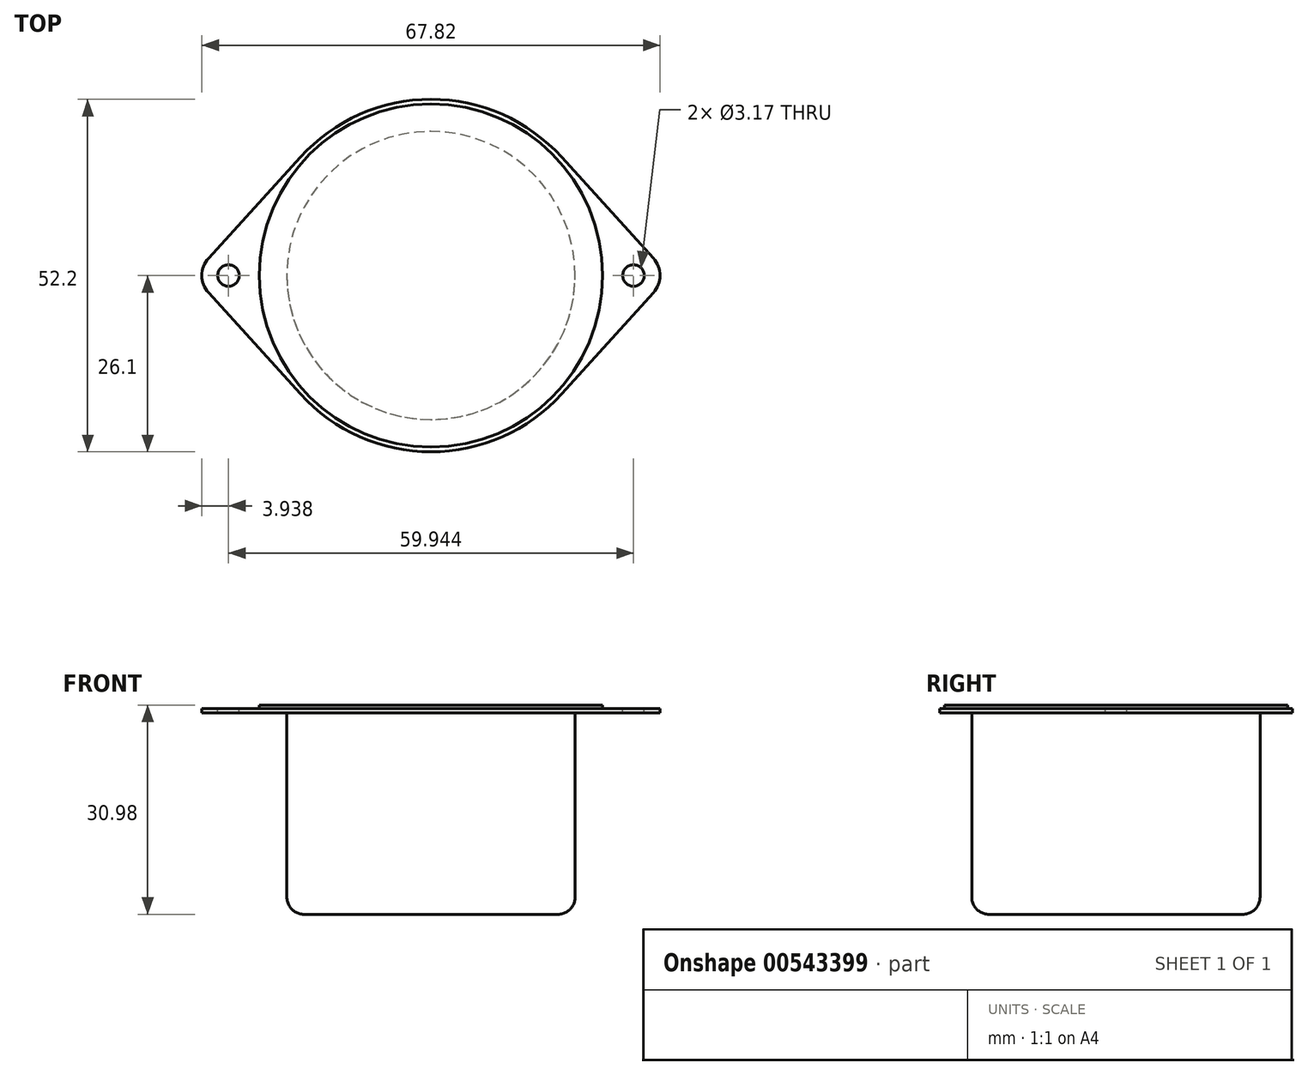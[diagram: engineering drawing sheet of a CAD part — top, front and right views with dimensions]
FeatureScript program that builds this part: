
annotation { "Feature Type Name" : "Feature", "Feature Type Description" : "" }
export const myFeature = defineFeature(function(context is Context, id is Id, definition is map)
    precondition{}
    {
        {
            var Q0;
            Q0=qCreatedBy(makeId("Front.planeOp"),FACE);
            var sketch = newSketch(context, id + "F0", { "sketchPlane" : qUnion([Q0])});
            skLineSegment(sketch, "E0", {"start": v(0, 46.59) * mm, "end": v(0, -54.94) * mm, "construction": true});
            skLineSegment(sketch, "E1", {"start": v(26.1, 14.99) * mm, "end": v(26.1, 14.35) * mm});
            skLineSegment(sketch, "E2", {"start": v(26.1, 14.35) * mm, "end": v(21.34, 14.35) * mm});
            skLineSegment(sketch, "E3", {"start": v(21.34, 14.35) * mm, "end": v(21.34, -15.5) * mm});
            skLineSegment(sketch, "E4", {"start": v(21.34, -15.5) * mm, "end": v(0, -15.5) * mm});
            skLineSegment(sketch, "E5", {"start": v(0, -15.5) * mm, "end": v(0, 15.5) * mm});
            skLineSegment(sketch, "E6", {"start": v(26.1, 14.99) * mm, "end": v(25.4, 14.99) * mm});
            skLineSegment(sketch, "E7", {"start": v(25.4, 14.99) * mm, "end": v(25.4, 15.5) * mm});
            skLineSegment(sketch, "E8", {"start": v(25.4, 15.5) * mm, "end": v(0, 15.5) * mm});
            skPoint(sketch, "E9.6.internal.snap0", {"position": v(12.7, 15.5) * mm});
            skSolve(sketch);
        }
        {
            var Q0;
            Q0 = qSketchRegion(id + "F0", true);
            var Q1;
            Q1=sQuery(id+"F0.wireOp",EDGE,"E0");
            revolve(context, id + "F1", {"entities" : qUnion([Q0]), "axis" : qUnion([Q1]), "revolveType" : RevolveType.FULL});
        }
        {
            var Q0;
            Q0=makeQuery(id+"F1.opRevolve","SWEPT_FACE",FACE,{"disambiguationData":[OSD([sQuery(id+"F0.wireOp",EDGE,"E6")])]});
            var sketch = newSketch(context, id + "F2", { "sketchPlane" : qUnion([Q0])});
            skCircle(sketch, "E10.0", {"center": v(0, 0) * mm, "radius": 26.1 * mm});
            skCircle(sketch, "E11", {"center": v(-30.1, 0) * mm, "radius": 3.81 * mm});
            skCircle(sketch, "E12", {"center": v(30.1, 0) * mm, "radius": 3.81 * mm});
            skLineSegment(sketch, "E13", {"start": v(-32.92, 2.56) * mm, "end": v(-19.33, 17.54) * mm});
            skLineSegment(sketch, "E14", {"start": v(-32.92, -2.56) * mm, "end": v(-19.33, -17.54) * mm});
            skLineSegment(sketch, "E15", {"start": v(32.92, -2.56) * mm, "end": v(19.33, -17.54) * mm});
            skLineSegment(sketch, "E16", {"start": v(32.92, 2.56) * mm, "end": v(19.33, 17.54) * mm});
            skLineSegment(sketch, "E17", {"start": v(0, 37.88) * mm, "end": v(0, -40.1) * mm, "construction": true});
            skCircle(sketch, "E18", {"center": v(-29.97, 0) * mm, "radius": 1.59 * mm});
            skCircle(sketch, "E19", {"center": v(29.97, 0) * mm, "radius": 1.59 * mm});
            skSolve(sketch);
        }
        {
            var Q0;
            Q0 = qSketchRegion(id + "F2", true);
            var Q1;
            Q1=makeQuery(id+"F1.opRevolve","SWEPT_FACE",FACE,{"disambiguationData":[OSD([sQuery(id+"F0.wireOp",EDGE,"E2")])]});
            extrude(context, id + "F3", {"entities" : qUnion([Q0]), "operationType" : NewBodyOperationType.ADD, "endBound" : BoundingType.UP_TO_SURFACE, "oppositeDirection" : true, "depth" : 25.4 * mm, "endBoundEntityFace" : qUnion([Q1]), "offsetDistance" : 25.4 * mm});
        }
        {
            var Q0;
            Q0=makeQuery(id+"F1.opRevolve","SWEPT_EDGE",EDGE,{"disambiguationData":[OSD([sQuery(id+"F0.wireOp",EDGE,"E3"),sQuery(id+"F0.wireOp",EDGE,"E4")])]});
            fillet(context, id + "F4", {"entities" : qUnion([Q0]), "radius" : 2.54 * mm, "tangentPropagation" : true, "allowEdgeOverflow" : false});
        }
    });
